# Revit family: Hager-Golf-IP40-Plain_Door-sistema-NoHosted-ES-es
name_source: partatom
category: Electrical Equipment
units: mm (PartAtom-declared; Revit-internal decimal feet)

## family parameters
Always vertical = Yes
Cut with Voids When Loaded = No
Panel Configuration = Two Columns, Circuits Across
Part Type = Panelboard
Room Calculation Point = No
Round Connector Dimension = Use Diameter
Shared = No
Work Plane-Based = Yes

## types (43) — shared parameters
Default Elevation = 1219 mm
EF000007 - Color = EV000202 - Blanco
EF000116 - Número RAL = 9010
EF000118 - Con placa de montaje = No
EF000339 - Tipo de cubierta = EV004216 - Puerta
EF001062 - Versión de EMC = No
EF001088 - Posibilidad de extensión = Yes
EF001134 - Carril DIN = Yes
EF001596 - Material de la carcasa = EV000139 - Plástico
EF004462 - Tipo de cierre = EV000154 - Otros
EF006244 - Tapa/puerta transparente = No
EF006306 - Con cierre = No
EF009212 - Versión de la cubierta = EV000116 - Cerrado
EF015941 - Puerta de transmisión de señal = Yes
HG000001 - Número de columnas = 1
HG000002 - Con puerta o tapa = Yes
HG000003 - Gama = Golf
HG000005 - Grosor = 3 mm  [stored 0.00984252 ft]
HG000009 - Puerta batiente doble = No
HG000010 - Puertas asimétricas = No
HG000011 - Filas vacías desde abajo = No
HG000017 - Distancia entre polos = 18 mm  [stored 0.0590551 ft]
Manufacturer = Hager
Type Comments = Golf
zero-valued in all types: HG000007 - Número de columnas vacías, HG000008 - Número de filas vacías

## per-type parameters (varying)
| type | EF000003 - Tipo de montaje | EF000008 - Anchura | EF000040 - Altura | EF000049 - Profundidad | EF000218 - Profundidad de instalación | EF000266 - Número de filas | EF000332 - Altura de la instalación | EF000846 - Anchura de instalación | EF001131 - Profundidad interna | EF002950 - Anchura de unidades de división | EF005474 - Grado de protección (IP) | EF015776 - Borne de tierra | EF015777 - Borne neutro | HG000004 - Referencia del fabricante | HG000006 - Empotrado | Model |
| Montado empotrado  A204 A225 P97.5 4 unidad de división - VF104PE | EV000383 - Montado empotrado (escayola) | 204 mm | 225 mm  [stored 0.738189 ft] | 98 mm  [stored 0.321522 ft] | 72 mm  [stored 0.23622 ft] | 1 | 189 mm  [stored 0.620079 ft] | 170 mm  [stored 0.557743 ft] | 98 mm  [stored 0.321522 ft] | 4 |  | Yes | No | VF104PE | Yes | VF104PE |
| Montado empotrado  A204 A225 P97.5 4 unidad de división - VF104PEB | EV000128 - Pared hueca | 204 mm | 225 mm  [stored 0.738189 ft] | 98 mm  [stored 0.321522 ft] | 72 mm  [stored 0.23622 ft] | 1 | 189 mm  [stored 0.620079 ft] | 170 mm  [stored 0.557743 ft] | 98 mm  [stored 0.321522 ft] | 4 |  | No | No | VF104PEB | Yes | VF104PEB |
| Montado empotrado  A204 A225 P97.5 4 unidad de división - VF104PEH | EV000383 - Montado empotrado (escayola) | 204 mm | 225 mm  [stored 0.738189 ft] | 98 mm  [stored 0.321522 ft] | 72 mm  [stored 0.23622 ft] | 1 | 189 mm  [stored 0.620079 ft] | 170 mm  [stored 0.557743 ft] | 98 mm  [stored 0.321522 ft] | 4 |  | Yes | No | VF104PEH | Yes | VF104PEH |
| Montado empotrado  A275 A225 P97.5 8 unidad de división - VF108PE | EV000383 - Montado empotrado (escayola) | 275 mm | 225 mm  [stored 0.738189 ft] | 98 mm  [stored 0.321522 ft] | 72 mm  [stored 0.23622 ft] | 1 | 189 mm  [stored 0.620079 ft] | 242 mm  [stored 0.793963 ft] | 98 mm  [stored 0.321522 ft] | 8 |  | Yes | No | VF108PE | Yes | VF108PE |
| Montado empotrado  A275 A225 P97.5 8 unidad de división - VF108PEB | EV000128 - Pared hueca | 275 mm | 225 mm  [stored 0.738189 ft] | 98 mm  [stored 0.321522 ft] | 72 mm  [stored 0.23622 ft] | 1 | 189 mm  [stored 0.620079 ft] | 242 mm  [stored 0.793963 ft] | 98 mm  [stored 0.321522 ft] | 8 |  | No | No | VF108PEB | Yes | VF108PEB |
| Montado empotrado  A275 A225 P97.5 8 unidad de división - VF108PEH | EV000383 - Montado empotrado (escayola) | 275 mm | 225 mm  [stored 0.738189 ft] | 98 mm  [stored 0.321522 ft] | 72 mm  [stored 0.23622 ft] | 1 | 189 mm  [stored 0.620079 ft] | 242 mm  [stored 0.793963 ft] | 98 mm  [stored 0.321522 ft] | 8 |  | Yes | No | VF108PEH | Yes | VF108PEH |
| Montado empotrado IP40 A352 A293 P97.5 12 unidad de división - VF112PE | EV000383 - Montado empotrado (escayola) | 352 mm  [stored 1.15486 ft] | 293 mm | 98 mm  [stored 0.321522 ft] | 72 mm  [stored 0.23622 ft] | 1 | 257 mm  [stored 0.843176 ft] | 318 mm  [stored 1.04331 ft] | 98 mm  [stored 0.321522 ft] | 12 | EV006415 - IP40 | Yes | No | VF112PE | Yes | VF112PE |
| Montado empotrado IP40 A352 A293 P97.5 12 unidad de división - VF112PEB | EV000128 - Pared hueca | 352 mm  [stored 1.15486 ft] | 293 mm | 98 mm  [stored 0.321522 ft] | 72 mm  [stored 0.23622 ft] | 1 | 257 mm  [stored 0.843176 ft] | 318 mm  [stored 1.04331 ft] | 98 mm  [stored 0.321522 ft] | 12 | EV006415 - IP40 | No | No | VF112PEB | Yes | VF112PEB |
| Montado empotrado IP40 A352 A293 P97.5 12 unidad de división - VF112PEH | EV000383 - Montado empotrado (escayola) | 352 mm  [stored 1.15486 ft] | 293 mm | 98 mm  [stored 0.321522 ft] | 72 mm  [stored 0.23622 ft] | 1 | 257 mm  [stored 0.843176 ft] | 318 mm  [stored 1.04331 ft] | 98 mm  [stored 0.321522 ft] | 12 | EV006415 - IP40 | Yes | No | VF112PEH | Yes | VF112PEH |
| Montado empotrado IP40 A352 A543 P97.5 12 unidad de división - VF312ICT | EV000383 - Montado empotrado (escayola) | 352 mm  [stored 1.15486 ft] | 543 mm  [stored 1.7815 ft] | 98 mm  [stored 0.321522 ft] | 72 mm  [stored 0.23622 ft] | 3 | 507 mm  [stored 1.66339 ft] | 318 mm  [stored 1.04331 ft] | 98 mm  [stored 0.321522 ft] | 12 | EV006415 - IP40 | No | No | VF312ICT | Yes | VF312ICT |
| Montado empotrado IP40 A352 A543 P97.5 12 unidad de división - VF312PE | EV000383 - Montado empotrado (escayola) | 352 mm  [stored 1.15486 ft] | 543 mm  [stored 1.7815 ft] | 98 mm  [stored 0.321522 ft] | 72 mm  [stored 0.23622 ft] | 3 | 507 mm  [stored 1.66339 ft] | 318 mm  [stored 1.04331 ft] | 98 mm  [stored 0.321522 ft] | 12 | EV006415 - IP40 | Yes | No | VF312PE | Yes | VF312PE |
| Montado empotrado IP40 A352 A543 P97.5 12 unidad de división - VF312PEB | EV000128 - Pared hueca | 352 mm  [stored 1.15486 ft] | 543 mm  [stored 1.7815 ft] | 98 mm  [stored 0.321522 ft] | 72 mm  [stored 0.23622 ft] | 3 | 507 mm  [stored 1.66339 ft] | 318 mm  [stored 1.04331 ft] | 98 mm  [stored 0.321522 ft] | 12 | EV006415 - IP40 | No | No | VF312PEB | Yes | VF312PEB |
| Montado empotrado IP40 A352 A543 P97.5 12 unidad de división - VF312PEBH | EV000128 - Pared hueca | 352 mm  [stored 1.15486 ft] | 543 mm  [stored 1.7815 ft] | 98 mm  [stored 0.321522 ft] | 72 mm  [stored 0.23622 ft] | 3 | 507 mm  [stored 1.66339 ft] | 318 mm  [stored 1.04331 ft] | 98 mm  [stored 0.321522 ft] | 12 | EV006415 - IP40 | No | Yes | VF312PEBH | Yes | VF312PEBH |
| Montado empotrado IP40 A352 A543 P97.5 12 unidad de división - VF312PEH | EV000383 - Montado empotrado (escayola) | 352 mm  [stored 1.15486 ft] | 543 mm  [stored 1.7815 ft] | 98 mm  [stored 0.321522 ft] | 72 mm  [stored 0.23622 ft] | 3 | 507 mm  [stored 1.66339 ft] | 318 mm  [stored 1.04331 ft] | 98 mm  [stored 0.321522 ft] | 12 | EV006415 - IP40 | Yes | No | VF312PEH | Yes | VF312PEH |
| Montado empotrado IP40 A352 A688 P97.5 12 unidad de división - VF412PE | EV000383 - Montado empotrado (escayola) | 352 mm  [stored 1.15486 ft] | 688 mm  [stored 2.25722 ft] | 98 mm  [stored 0.321522 ft] | 72 mm  [stored 0.23622 ft] | 4 | 652 mm  [stored 2.13911 ft] | 318 mm  [stored 1.04331 ft] | 98 mm  [stored 0.321522 ft] | 12 | EV006415 - IP40 | Yes | No | VF412PE | Yes | VF412PE |
| Montado empotrado IP40 A352 A688 P97.5 12 unidad de división - VF412PEB | EV000128 - Pared hueca | 352 mm  [stored 1.15486 ft] | 688 mm  [stored 2.25722 ft] | 98 mm  [stored 0.321522 ft] | 72 mm  [stored 0.23622 ft] | 4 | 652 mm  [stored 2.13911 ft] | 318 mm  [stored 1.04331 ft] | 98 mm  [stored 0.321522 ft] | 12 | EV006415 - IP40 | No | No | VF412PEB | Yes | VF412PEB |
| Montado empotrado IP40 A352 A688 P97.5 12 unidad de división - VF412PEBH | EV000128 - Pared hueca | 352 mm  [stored 1.15486 ft] | 688 mm  [stored 2.25722 ft] | 98 mm  [stored 0.321522 ft] | 72 mm  [stored 0.23622 ft] | 4 | 652 mm  [stored 2.13911 ft] | 318 mm  [stored 1.04331 ft] | 98 mm  [stored 0.321522 ft] | 12 | EV006415 - IP40 | No | Yes | VF412PEBH | Yes | VF412PEBH |
| Montado empotrado IP40 A352 A688 P97.5 12 unidad de división - VF412PEH | EV000383 - Montado empotrado (escayola) | 352 mm  [stored 1.15486 ft] | 688 mm  [stored 2.25722 ft] | 98 mm  [stored 0.321522 ft] | 72 mm  [stored 0.23622 ft] | 4 | 652 mm  [stored 2.13911 ft] | 318 mm  [stored 1.04331 ft] | 98 mm  [stored 0.321522 ft] | 12 | EV006415 - IP40 | Yes | No | VF412PEH | Yes | VF412PEH |
| Montado empotrado IP40 A382 A418 P97.5 12 unidad de división - VF212PE | EV000383 - Montado empotrado (escayola) | 382 mm  [stored 1.25328 ft] | 418 mm  [stored 1.37139 ft] | 98 mm  [stored 0.321522 ft] | 72 mm  [stored 0.23622 ft] | 2 | 382 mm  [stored 1.25328 ft] | 318 mm  [stored 1.04331 ft] | 98 mm  [stored 0.321522 ft] | 12 | EV006415 - IP40 | Yes | No | VF212PE | Yes | VF212PE |
| Montado empotrado IP40 A382 A418 P97.5 12 unidad de división - VF212PEB | EV000128 - Pared hueca | 382 mm  [stored 1.25328 ft] | 418 mm  [stored 1.37139 ft] | 98 mm  [stored 0.321522 ft] | 72 mm  [stored 0.23622 ft] | 2 | 382 mm  [stored 1.25328 ft] | 318 mm  [stored 1.04331 ft] | 98 mm  [stored 0.321522 ft] | 12 | EV006415 - IP40 | No | No | VF212PEB | Yes | VF212PEB |
| Montado empotrado IP40 A382 A418 P97.5 12 unidad de división - VF212PEH | EV000383 - Montado empotrado (escayola) | 382 mm  [stored 1.25328 ft] | 418 mm  [stored 1.37139 ft] | 98 mm  [stored 0.321522 ft] | 72 mm  [stored 0.23622 ft] | 2 | 382 mm  [stored 1.25328 ft] | 318 mm  [stored 1.04331 ft] | 98 mm  [stored 0.321522 ft] | 12 | EV006415 - IP40 | Yes | No | VF212PEH | Yes | VF212PEH |
| Montado empotrado IP40 A460 A293 P97.5 18 unidad de división - VF118PEH | EV000383 - Montado empotrado (escayola) | 460 mm  [stored 1.50919 ft] | 293 mm | 98 mm  [stored 0.321522 ft] | 72 mm  [stored 0.23622 ft] | 1 | 257 mm  [stored 0.843176 ft] | 426 mm  [stored 1.39764 ft] | 98 mm  [stored 0.321522 ft] | 18 | EV006415 - IP40 | Yes | No | VF118PEH | Yes | VF118PEH |
| Montado empotrado IP40 A460 A293 P97.5 18 unidad de división - VF118PES | EV000383 - Montado empotrado (escayola) | 460 mm  [stored 1.50919 ft] | 293 mm | 98 mm  [stored 0.321522 ft] | 72 mm  [stored 0.23622 ft] | 1 | 257 mm  [stored 0.843176 ft] | 426 mm  [stored 1.39764 ft] | 98 mm  [stored 0.321522 ft] | 18 | EV006415 - IP40 | No | No | VF118PES | Yes | VF118PES |
| Montado empotrado IP40 A460 A418 P97.5 18 unidad de división - VF218PEH | EV000383 - Montado empotrado (escayola) | 460 mm  [stored 1.50919 ft] | 418 mm  [stored 1.37139 ft] | 98 mm  [stored 0.321522 ft] | 72 mm  [stored 0.23622 ft] | 2 | 382 mm  [stored 1.25328 ft] | 426 mm  [stored 1.39764 ft] | 98 mm  [stored 0.321522 ft] | 18 | EV006415 - IP40 | Yes | No | VF218PEH | Yes | VF218PEH |
| Montado empotrado IP40 A460 A418 P97.5 18 unidad de división - VF218PES | EV000383 - Montado empotrado (escayola) | 460 mm  [stored 1.50919 ft] | 418 mm  [stored 1.37139 ft] | 98 mm  [stored 0.321522 ft] | 72 mm  [stored 0.23622 ft] | 2 | 382 mm  [stored 1.25328 ft] | 426 mm  [stored 1.39764 ft] | 98 mm  [stored 0.321522 ft] | 18 | EV006415 - IP40 | No | No | VF218PES | Yes | VF218PES |
| Montado empotrado IP40 A460 A543 P97.5 18 unidad de división - VF318PEH | EV000383 - Montado empotrado (escayola) | 460 mm  [stored 1.50919 ft] | 543 mm  [stored 1.7815 ft] | 98 mm  [stored 0.321522 ft] | 72 mm  [stored 0.23622 ft] | 3 | 507 mm  [stored 1.66339 ft] | 426 mm  [stored 1.39764 ft] | 98 mm  [stored 0.321522 ft] | 18 | EV006415 - IP40 | Yes | No | VF318PEH | Yes | VF318PEH |
| Montado empotrado IP40 A460 A543 P97.5 18 unidad de división - VF318PES | EV000383 - Montado empotrado (escayola) | 460 mm  [stored 1.50919 ft] | 543 mm  [stored 1.7815 ft] | 98 mm  [stored 0.321522 ft] | 72 mm  [stored 0.23622 ft] | 3 | 507 mm  [stored 1.66339 ft] | 426 mm  [stored 1.39764 ft] | 98 mm  [stored 0.321522 ft] | 18 | EV006415 - IP40 | No | No | VF318PES | Yes | VF318PES |
| Montado empotrado IP40 A460 A688 P97.5 18 unidad de división - VF418PEH | EV000383 - Montado empotrado (escayola) | 460 mm  [stored 1.50919 ft] | 688 mm  [stored 2.25722 ft] | 98 mm  [stored 0.321522 ft] | 72 mm  [stored 0.23622 ft] | 4 | 652 mm  [stored 2.13911 ft] | 426 mm  [stored 1.39764 ft] | 98 mm  [stored 0.321522 ft] | 18 | EV006415 - IP40 | Yes | No | VF418PEH | Yes | VF418PEH |
| Montado empotrado IP40 A460 A688 P97.5 18 unidad de división - VF418PES | EV000383 - Montado empotrado (escayola) | 460 mm  [stored 1.50919 ft] | 688 mm  [stored 2.25722 ft] | 98 mm  [stored 0.321522 ft] | 72 mm  [stored 0.23622 ft] | 4 | 652 mm  [stored 2.13911 ft] | 426 mm  [stored 1.39764 ft] | 98 mm  [stored 0.321522 ft] | 18 | EV006415 - IP40 | No | No | VF418PES | Yes | VF418PES |
| Montado superficial  A138 A184 P99 4 unidad de división - VS104PE | EV000384 - Montado superficial (escayola) | 138 mm  [stored 0.452756 ft] | 184 mm  [stored 0.603675 ft] | 99 mm  [stored 0.324803 ft] | 0 mm  [stored 0 ft] | 1 | 0 mm  [stored 0 ft] | 0 mm  [stored 0 ft] | 99 mm  [stored 0.324803 ft] | 4 |  | Yes | No | VS104PE | No | VS104PE |
| Montado superficial  A138 A184 P99 4 unidad de división - VS104PEB | EV000384 - Montado superficial (escayola) | 138 mm  [stored 0.452756 ft] | 184 mm  [stored 0.603675 ft] | 99 mm  [stored 0.324803 ft] | 0 mm  [stored 0 ft] | 1 | 0 mm  [stored 0 ft] | 0 mm  [stored 0 ft] | 99 mm  [stored 0.324803 ft] | 4 |  | No | No | VS104PEB | No | VS104PEB |
| Montado superficial  A210 A184 P99 8 unidad de división - VS108PE | EV000384 - Montado superficial (escayola) | 210 mm  [stored 0.688976 ft] | 184 mm  [stored 0.603675 ft] | 99 mm  [stored 0.324803 ft] | 0 mm  [stored 0 ft] | 1 | 0 mm  [stored 0 ft] | 0 mm  [stored 0 ft] | 99 mm  [stored 0.324803 ft] | 8 |  | Yes | No | VS108PE | No | VS108PE |
| Montado superficial  A210 A184 P99 8 unidad de división - VS108PEB | EV000384 - Montado superficial (escayola) | 210 mm  [stored 0.688976 ft] | 184 mm  [stored 0.603675 ft] | 99 mm  [stored 0.324803 ft] | 0 mm  [stored 0 ft] | 1 | 0 mm  [stored 0 ft] | 0 mm  [stored 0 ft] | 99 mm  [stored 0.324803 ft] | 8 |  | No | No | VS108PEB | No | VS108PEB |
| Montado superficial IP40 A282 A252 P99 12 unidad de división - VS112PE | EV000384 - Montado superficial (escayola) | 282 mm | 252 mm  [stored 0.826772 ft] | 99 mm  [stored 0.324803 ft] | 0 mm  [stored 0 ft] | 1 | 0 mm  [stored 0 ft] | 0 mm  [stored 0 ft] | 99 mm  [stored 0.324803 ft] | 12 | EV006415 - IP40 | Yes | No | VS112PE | No | VS112PE |
| Montado superficial IP40 A282 A252 P99 12 unidad de división - VS112PEB | EV000384 - Montado superficial (escayola) | 282 mm | 252 mm  [stored 0.826772 ft] | 99 mm  [stored 0.324803 ft] | 0 mm  [stored 0 ft] | 1 | 0 mm  [stored 0 ft] | 0 mm  [stored 0 ft] | 99 mm  [stored 0.324803 ft] | 12 | EV006415 - IP40 | No | No | VS112PEB | No | VS112PEB |
| Montado superficial IP40 A282 A377 P99 12 unidad de división - VS212PE | EV000384 - Montado superficial (escayola) | 282 mm | 377 mm  [stored 1.23688 ft] | 99 mm  [stored 0.324803 ft] | 0 mm  [stored 0 ft] | 2 | 0 mm  [stored 0 ft] | 0 mm  [stored 0 ft] | 99 mm  [stored 0.324803 ft] | 12 | EV006415 - IP40 | Yes | No | VS212PE | No | VS212PE |
| Montado superficial IP40 A282 A377 P99 12 unidad de división - VS212PEB | EV000384 - Montado superficial (escayola) | 282 mm | 377 mm  [stored 1.23688 ft] | 99 mm  [stored 0.324803 ft] | 0 mm  [stored 0 ft] | 2 | 0 mm  [stored 0 ft] | 0 mm  [stored 0 ft] | 99 mm  [stored 0.324803 ft] | 12 | EV006415 - IP40 | No | No | VS212PEB | No | VS212PEB |
| Montado superficial IP40 A282 A500 P99 12 unidad de división - VS312PE | EV000384 - Montado superficial (escayola) | 282 mm | 500 mm  [stored 1.64042 ft] | 99 mm  [stored 0.324803 ft] | 0 mm  [stored 0 ft] | 3 | 0 mm  [stored 0 ft] | 0 mm  [stored 0 ft] | 99 mm  [stored 0.324803 ft] | 12 | EV006415 - IP40 | Yes | No | VS312PE | No | VS312PE |
| Montado superficial IP40 A282 A647 P99 12 unidad de división - VS412PE | EV000384 - Montado superficial (escayola) | 282 mm | 647 mm  [stored 2.1227 ft] | 99 mm  [stored 0.324803 ft] | 0 mm  [stored 0 ft] | 4 | 0 mm  [stored 0 ft] | 0 mm  [stored 0 ft] | 99 mm  [stored 0.324803 ft] | 12 | EV006415 - IP40 | Yes | No | VS412PE | No | VS412PE |
| Montado superficial IP40 A390 A252 P99 18 unidad de división - VS118PES | EV000384 - Montado superficial (escayola) | 390 mm  [stored 1.27953 ft] | 252 mm  [stored 0.826772 ft] | 99 mm  [stored 0.324803 ft] | 0 mm  [stored 0 ft] | 1 | 0 mm  [stored 0 ft] | 0 mm  [stored 0 ft] | 99 mm  [stored 0.324803 ft] | 18 | EV006415 - IP40 | No | No | VS118PES | No | VS118PES |
| Montado superficial IP40 A390 A377 P99 18 unidad de división - VS218PES | EV000384 - Montado superficial (escayola) | 390 mm  [stored 1.27953 ft] | 377 mm  [stored 1.23688 ft] | 99 mm  [stored 0.324803 ft] | 0 mm  [stored 0 ft] | 2 | 0 mm  [stored 0 ft] | 0 mm  [stored 0 ft] | 99 mm  [stored 0.324803 ft] | 18 | EV006415 - IP40 | No | No | VS218PES | No | VS218PES |
| Montado superficial IP40 A390 A500 P99 18 unidad de división - VS318PES | EV000384 - Montado superficial (escayola) | 390 mm  [stored 1.27953 ft] | 500 mm  [stored 1.64042 ft] | 99 mm  [stored 0.324803 ft] | 0 mm  [stored 0 ft] | 3 | 0 mm  [stored 0 ft] | 0 mm  [stored 0 ft] | 99 mm  [stored 0.324803 ft] | 18 | EV006415 - IP40 | No | No | VS318PES | No | VS318PES |
| Montado superficial IP40 A390 A647 P99 18 unidad de división - VS418PES | EV000384 - Montado superficial (escayola) | 390 mm  [stored 1.27953 ft] | 647 mm  [stored 2.1227 ft] | 99 mm  [stored 0.324803 ft] | 0 mm  [stored 0 ft] | 4 | 0 mm  [stored 0 ft] | 0 mm  [stored 0 ft] | 99 mm  [stored 0.324803 ft] | 18 | EV006415 - IP40 | No | No | VS418PES | No | VS418PES |

note: [stored X ft] marks values corroborated as IEEE doubles in the binary element streams (Revit-internal decimal feet)

## geometry (parser evidence)
native form markers: Sweep x13
no freeform markers — native parametric forms only
